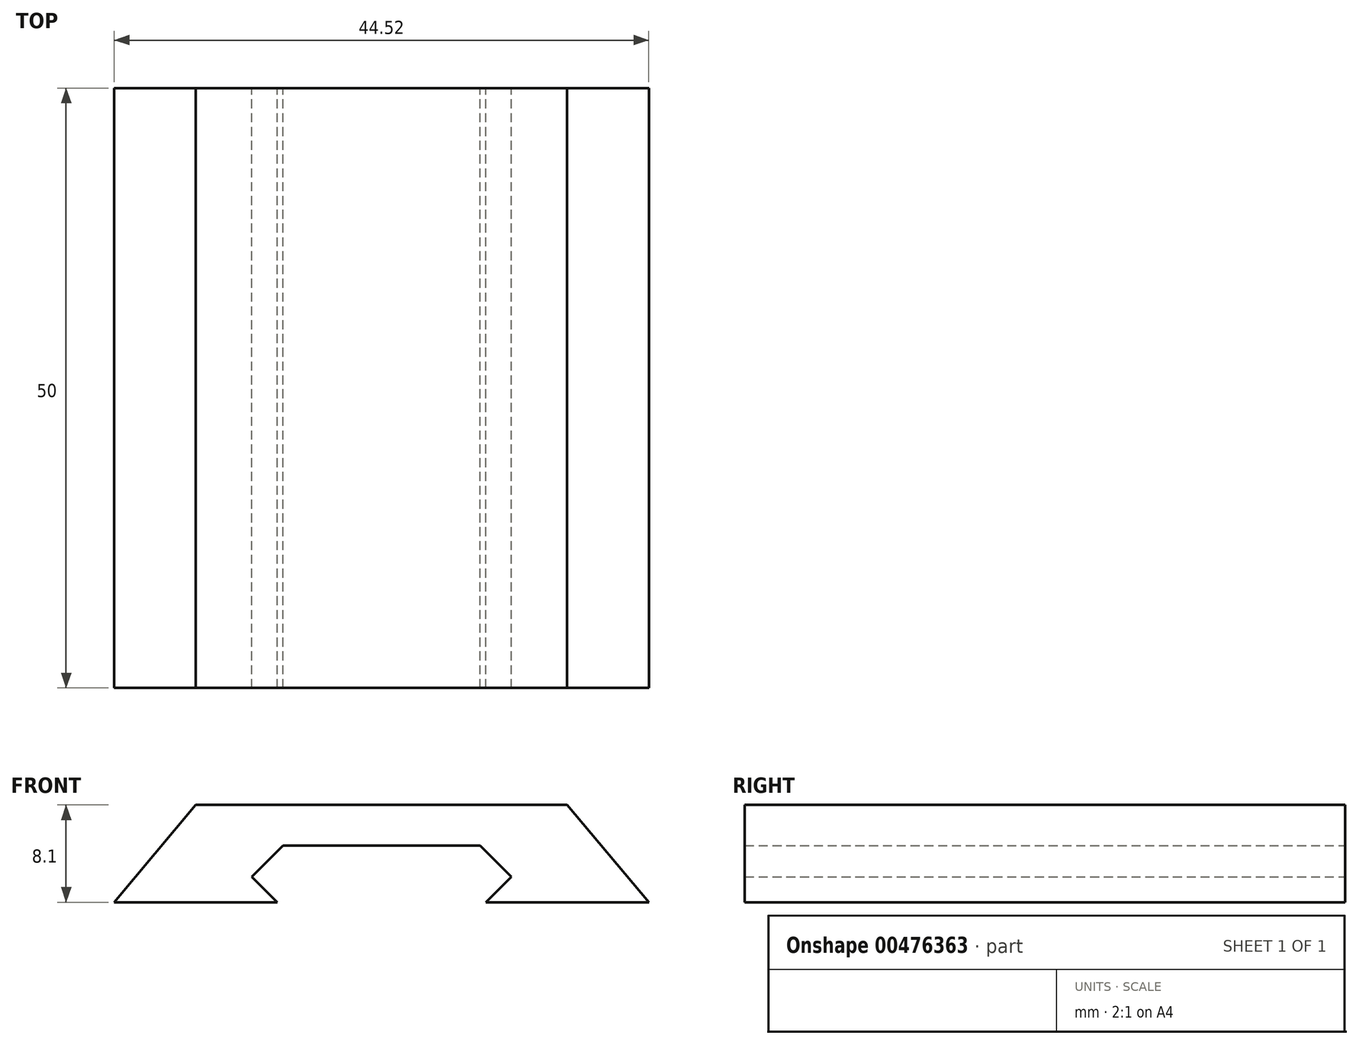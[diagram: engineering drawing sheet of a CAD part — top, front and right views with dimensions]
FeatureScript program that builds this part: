
annotation { "Feature Type Name" : "Feature", "Feature Type Description" : "" }
export const myFeature = defineFeature(function(context is Context, id is Id, definition is map)
    precondition{}
    {
        {
            var Q0;
            Q0=qCreatedBy(makeId("Front.planeOp"),FACE);
            var sketch = newSketch(context, id + "F0", { "sketchPlane" : qUnion([Q0])});
            skLineSegment(sketch, "E0", {"start": v(-8.2, -3.38) * mm, "end": v(-10.8, -5.98) * mm});
            skLineSegment(sketch, "E1.MirrorCS", {"start": v(8.2, -3.38) * mm, "end": v(10.8, -5.98) * mm});
            skLineSegment(sketch, "E2", {"start": v(-10.8, -5.98) * mm, "end": v(-8.68, -8.1) * mm});
            skLineSegment(sketch, "E3", {"start": v(-15.47, 0) * mm, "end": v(15.47, 0) * mm});
            skLineSegment(sketch, "E4", {"start": v(8.2, -3.38) * mm, "end": v(-8.2, -3.38) * mm});
            skLineSegment(sketch, "E5", {"start": v(8.68, -8.1) * mm, "end": v(22.26, -8.1) * mm});
            skLineSegment(sketch, "E6", {"start": v(15.47, 0) * mm, "end": v(22.26, -8.1) * mm});
            skLineSegment(sketch, "E7.MirrorCS", {"start": v(-15.47, 0) * mm, "end": v(-22.26, -8.1) * mm});
            skLineSegment(sketch, "E8.MirrorCS", {"start": v(-8.68, -8.1) * mm, "end": v(-22.26, -8.1) * mm});
            skLineSegment(sketch, "E9", {"start": v(8.68, -8.1) * mm, "end": v(10.8, -5.98) * mm});
            skLineSegment(sketch, "E10", {"start": v(-8.2, -3.38) * mm, "end": v(0, -3.38) * mm});
            skLineSegment(sketch, "E11", {"start": v(0, -3.38) * mm, "end": v(0, 0) * mm});
            skSolve(sketch);
        }
        {
            var Q0;
            Q0 = qSketchRegion(id + "F0", true);
            extrude(context, id + "F1", {"entities" : qUnion([Q0]), "depth" : 50 * mm});
        }
    });
